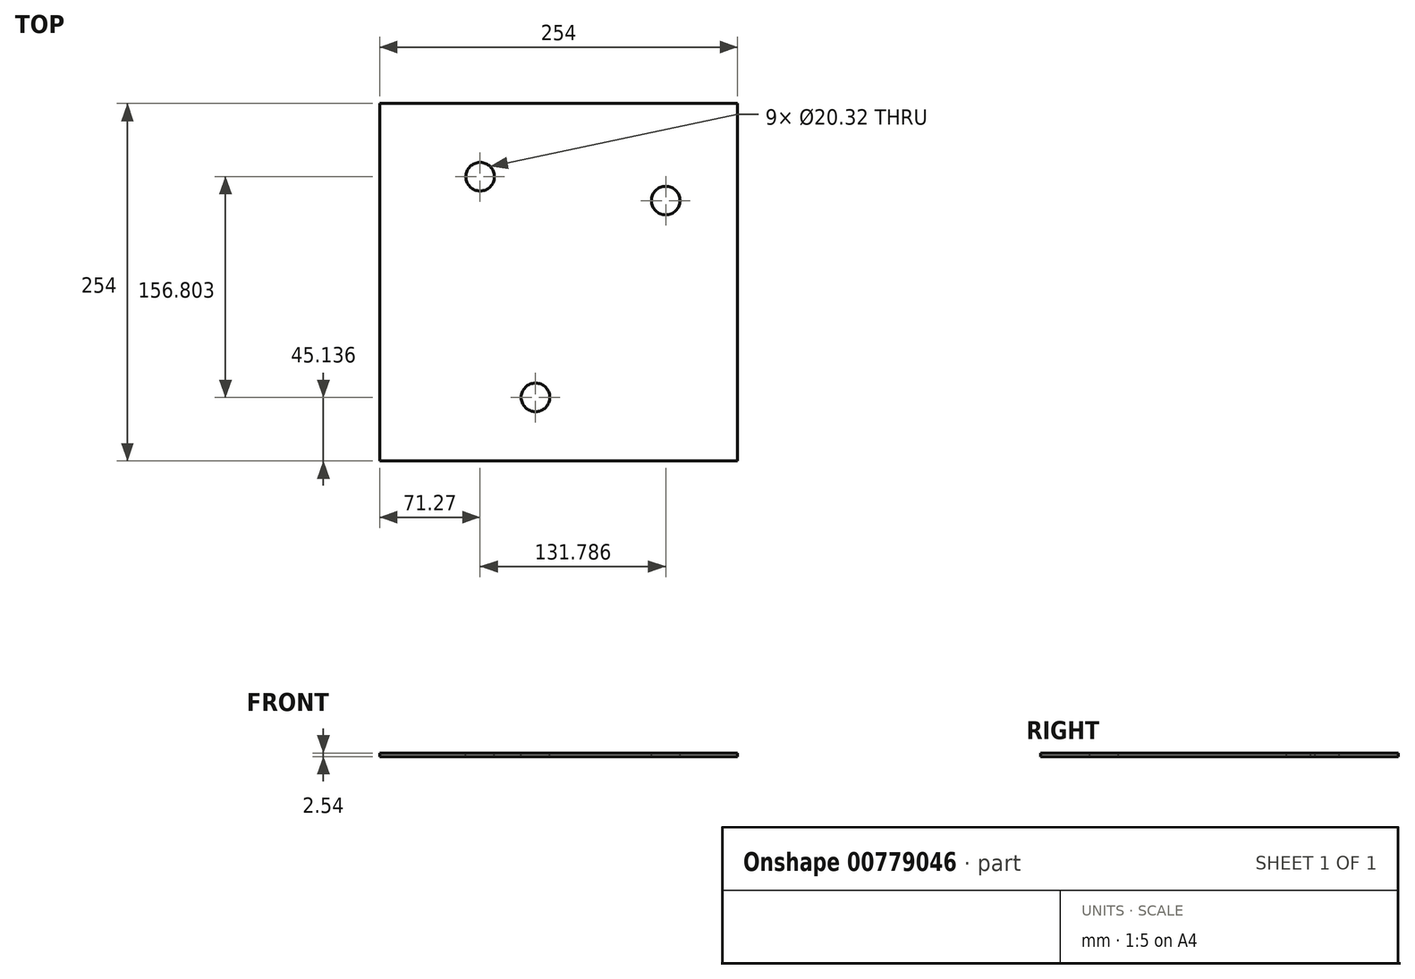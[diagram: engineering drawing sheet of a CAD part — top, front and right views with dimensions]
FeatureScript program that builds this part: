
annotation { "Feature Type Name" : "Feature", "Feature Type Description" : "" }
export const myFeature = defineFeature(function(context is Context, id is Id, definition is map)
    precondition{}
    {
        {
            var Q0;
            Q0=qCreatedBy(makeId("Top.planeOp"),FACE);
            var sketch = newSketch(context, id + "F0", { "sketchPlane" : qUnion([Q0])});
            skLineSegment(sketch, "E0.bottom", {"start": v(127, 127) * mm, "end": v(-127, 127) * mm});
            skLineSegment(sketch, "E0.top", {"start": v(127, -127) * mm, "end": v(-127, -127) * mm});
            skLineSegment(sketch, "E0.left", {"start": v(127, 127) * mm, "end": v(127, -127) * mm});
            skLineSegment(sketch, "E0.right", {"start": v(-127, 127) * mm, "end": v(-127, -127) * mm});
            skPoint(sketch, "E0.middle", {"position": v(0, 0) * mm});
            skSolve(sketch);
        }
        {
            var Q0;
            Q0=makeQuery(id+"F0.imprint","IMPRINT",FACE,{"disambiguationData":[TD([[makeQuery(id+"F0.imprint","IMPRINT",EDGE,{"derivedFrom":sQuery(id+"F0.wireOp",EDGE,"E0.bottom")}),1.0]])]});
            extrude(context, id + "F1", {"entities" : qUnion([Q0]), "depth" : 2.54 * mm, "offsetDistance" : 25.4 * mm});
        }
        {
            var Q0;
            Q0=makeQuery(id+"F1.opExtrude","CAP_FACE",FACE,{"disambiguationData":[OSD([sQuery(id+"F0.wireOp",EDGE,"E0.bottom"),sQuery(id+"F0.wireOp",EDGE,"E0.top"),sQuery(id+"F0.wireOp",EDGE,"E0.left"),sQuery(id+"F0.wireOp",EDGE,"E0.right")])],"isStart":false});
            var sketch = newSketch(context, id + "F2", { "sketchPlane" : qUnion([Q0])});
            skPoint(sketch, "E1", {"position": v(-55.73, 74.94) * mm});
            skPoint(sketch, "E2", {"position": v(76.06, 57.96) * mm});
            skPoint(sketch, "E3", {"position": v(-16.42, -81.86) * mm});
            skSolve(sketch);
        }
        {
            var Q0;
            Q0=sQuery(id+"F2.wireOp",VERTEX,"E1");
            var Q1;
            Q1=sQuery(id+"F2.wireOp",VERTEX,"E2");
            var Q2;
            Q2=sQuery(id+"F2.wireOp",VERTEX,"E3");
            var Q3;
            Q3=makeQuery(id+"F1.opExtrude","SWEPT_BODY",BODY,{"disambiguationData":[OSD([sQuery(id+"F0.wireOp",EDGE,"E0.bottom"),sQuery(id+"F0.wireOp",EDGE,"E0.top"),sQuery(id+"F0.wireOp",EDGE,"E0.left"),sQuery(id+"F0.wireOp",EDGE,"E0.right")])]});
            hole(context, id + "F3", {"style" : HoleStyle.SIMPLE, "endStyle" : HoleEndStyle.THROUGH, "holeDiameter" : 20.32 * mm, "majorDiameter" : 6.35 * mm, "isTappedThrough" : true, "tappedDepth" : 12.7 * mm, "tapClearance" : 3, "locations" : qUnion([Q0, Q1, Q2]), "scope" : qUnion([Q3])});
        }
    });
